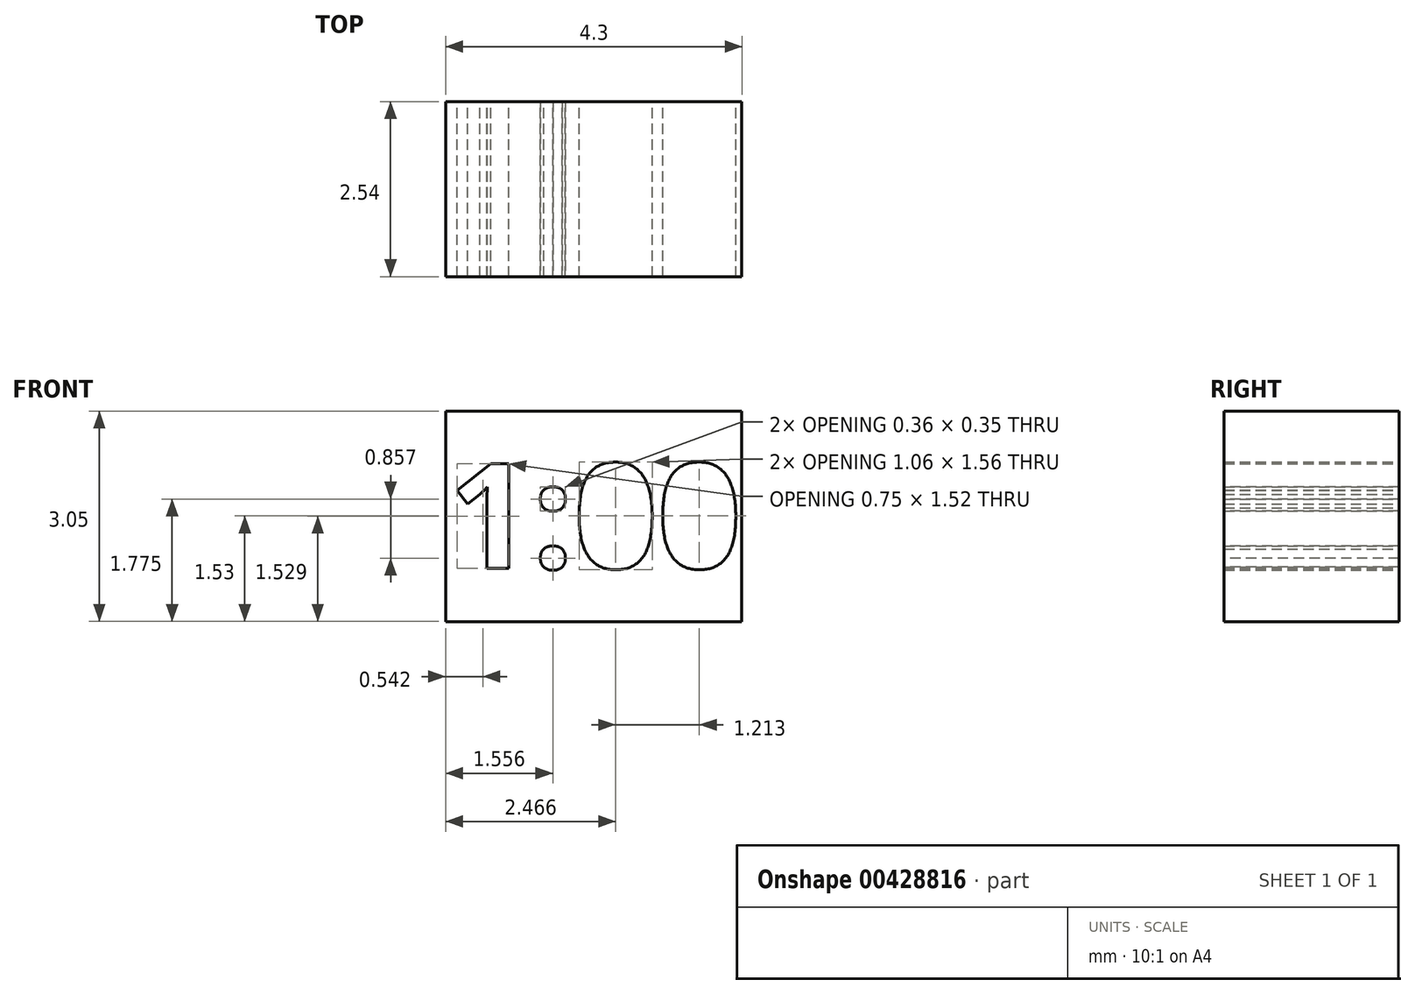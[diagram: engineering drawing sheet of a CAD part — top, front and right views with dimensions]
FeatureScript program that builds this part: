
annotation { "Feature Type Name" : "Feature", "Feature Type Description" : "" }
export const myFeature = defineFeature(function(context is Context, id is Id, definition is map)
    precondition{}
    {
        {
            var Q0;
            Q0=qCreatedBy(makeId("Front.planeOp"),FACE);
            var sketch = newSketch(context, id + "F0", { "sketchPlane" : qUnion([Q0])});
            skLineSegment(sketch, "E0.bottom", {"start": v(0, 0) * mm, "end": v(4.3, 0) * mm});
            skLineSegment(sketch, "E0.top", {"start": v(0, -3.05) * mm, "end": v(4.3, -3.05) * mm});
            skLineSegment(sketch, "E0.left", {"start": v(0, 0) * mm, "end": v(0, -3.05) * mm});
            skLineSegment(sketch, "E0.right", {"start": v(4.3, 0) * mm, "end": v(4.3, -3.05) * mm});
            skText(sketch, "E1", { "text": "1:00", "fontName": "OpenSans-Bold.ttf"});
            const initialGuessF0  = {"E1": [4e-05, -0.00228, 1, 0, 0.00153]};
            skSetInitialGuess(sketch, initialGuessF0);
            skSolve(sketch);
        }
        {
            var Q0;
            Q0 = qSketchRegion(id + "F0", true);
            extrude(context, id + "F1", {"entities" : qUnion([Q0]), "depth" : 2.54 * mm});
        }
    });
